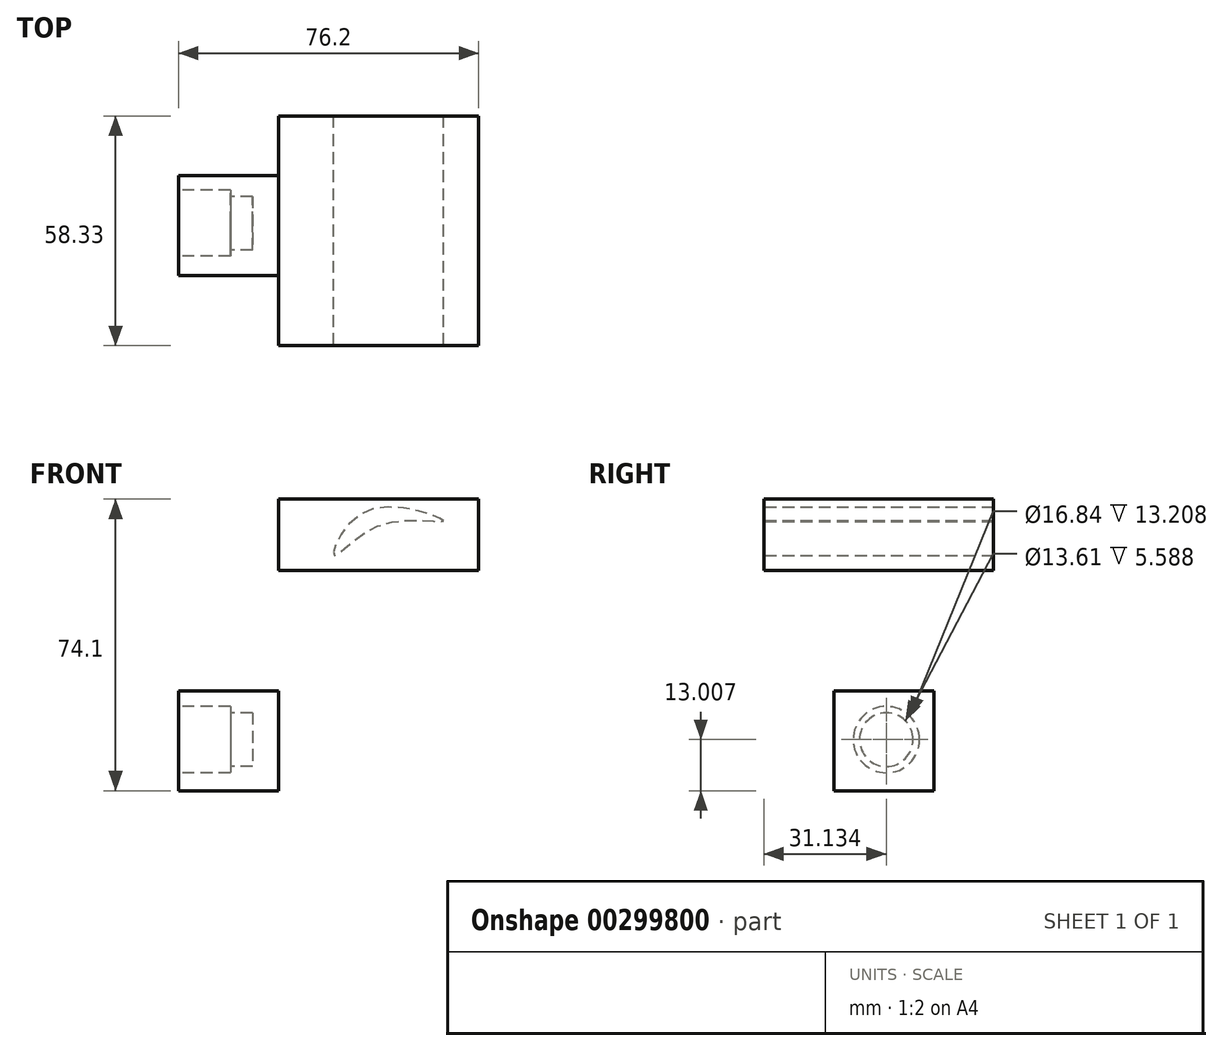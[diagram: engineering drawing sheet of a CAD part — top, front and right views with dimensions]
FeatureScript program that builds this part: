
annotation { "Feature Type Name" : "Feature", "Feature Type Description" : "" }
export const myFeature = defineFeature(function(context is Context, id is Id, definition is map)
    precondition{}
    {
        {
            var Q0;
            Q0=qCreatedBy(makeId("Front.planeOp"),FACE);
            var sketch = newSketch(context, id + "F0", { "sketchPlane" : qUnion([Q0])});
            skLineSegment(sketch, "E0", {"start": v(0, 25.4) * mm, "end": v(-25.4, 25.4) * mm});
            skLineSegment(sketch, "E1", {"start": v(0, 25.4) * mm, "end": v(0, 0) * mm});
            skLineSegment(sketch, "E2", {"start": v(0, 0) * mm, "end": v(-25.4, 0) * mm});
            skLineSegment(sketch, "E3", {"start": v(-25.4, 0) * mm, "end": v(-25.4, 25.4) * mm});
            skSolve(sketch);
        }
        {
            var Q0;
            Q0 = qSketchRegion(id + "F0", true);
            extrude(context, id + "F1", {"entities" : qUnion([Q0]), "depth" : 25.4 * mm});
        }
        {
            var Q0;
            Q0=makeQuery(id+"F0.imprint","IMPRINT",FACE,{"disambiguationData":[TD([[makeQuery(id+"F0.imprint","IMPRINT",EDGE,{"derivedFrom":sQuery(id+"F0.wireOp",EDGE,"E0")}),1.0]])]});
            extrude(context, id + "F2", {"entities" : qUnion([Q0]), "operationType" : NewBodyOperationType.ADD, "depth" : 25.4 * mm});
        }
        {
            var Q0;
            Q0=makeQuery(id+"F1.opExtrude","CAP_FACE",FACE,{"disambiguationData":[OSD([sQuery(id+"F0.wireOp",EDGE,"E0"),sQuery(id+"F0.wireOp",EDGE,"E1"),sQuery(id+"F0.wireOp",EDGE,"E2"),sQuery(id+"F0.wireOp",EDGE,"E3")])],"isStart":false});
            var sketch = newSketch(context, id + "F3", { "sketchPlane" : qUnion([Q0])});
            skCircle(sketch, "E4", {"center": v(-11.35, 11.82) * mm, "radius": 8.1 * mm});
            skCircle(sketch, "E5", {"center": v(-11.35, 11.82) * mm, "radius": 8.16 * mm});
            skSolve(sketch);
        }
        {
            var Q0;
            Q0 = qSketchRegion(id + "F3", true);
            var Q1;
            Q1=makeQuery(id+"F3.imprint","IMPRINT",FACE,{"disambiguationData":[TD([[makeQuery(id+"F3.imprint","IMPRINT",EDGE,{"derivedFrom":sQuery(id+"F3.wireOp",EDGE,"E4")}),1.0]])]});
            extrude(context, id + "F4", {"entities" : qUnion([Q0, Q1]), "operationType" : NewBodyOperationType.ADD, "oppositeDirection" : true, "depth" : 12.7 * mm});
        }
        {
            var Q0;
            Q0=makeQuery(id+"F1.opExtrude","SWEPT_FACE",FACE,{"disambiguationData":[OSD([sQuery(id+"F0.wireOp",EDGE,"E1")])]});
            var sketch = newSketch(context, id + "F5", { "sketchPlane" : qUnion([Q0])});
            skCircle(sketch, "E6", {"center": v(-13.12, 12.8) * mm, "radius": 9.62 * mm});
            skSolve(sketch);
        }
        {
            var Q0;
            Q0 = qSketchRegion(id + "F5", true);
            extrude(context, id + "F6", {"entities" : qUnion([Q0]), "operationType" : NewBodyOperationType.ADD, "oppositeDirection" : true, "depth" : 12.7 * mm});
        }
        {
            var Q0;
            Q0=makeQuery(id+"F1.opExtrude","SWEPT_FACE",FACE,{"disambiguationData":[OSD([sQuery(id+"F0.wireOp",EDGE,"E3")])]});
            var sketch = newSketch(context, id + "F7", { "sketchPlane" : qUnion([Q0])});
            skCircle(sketch, "E7", {"center": v(12.1, 13) * mm, "radius": 8.42 * mm});
            skSolve(sketch);
        }
        {
            var Q0;
            Q0 = qSketchRegion(id + "F7", true);
            extrude(context, id + "F8", {"entities" : qUnion([Q0]), "operationType" : NewBodyOperationType.REMOVE, "oppositeDirection" : true, "depth" : 13.2 * mm});
        }
        {
            var Q0;
            Q0=makeQuery(id+"F8.boolean.opBoolean","COPY",FACE,{"derivedFrom":makeQuery(id+"F8.opExtrude","CAP_FACE",FACE,{"disambiguationData":[OSD([sQuery(id+"F7.wireOp",EDGE,"E7")])],"isStart":false})});
            var sketch = newSketch(context, id + "F9", { "sketchPlane" : qUnion([Q0])});
            skCircle(sketch, "E8", {"center": v(12.1, 13) * mm, "radius": 6.8 * mm});
            skSolve(sketch);
        }
        {
            var Q0;
            Q0 = qSketchRegion(id + "F9", true);
            extrude(context, id + "F10", {"entities" : qUnion([Q0]), "operationType" : NewBodyOperationType.REMOVE, "oppositeDirection" : true, "depth" : 5.6 * mm});
        }
        {
            var Q0;
            Q0=qCreatedBy(makeId("Right.planeOp"),FACE);
            var sketch = newSketch(context, id + "F11", { "sketchPlane" : qUnion([Q0])});
            skLineSegment(sketch, "E9.bottom", {"start": v(-43.24, 55.97) * mm, "end": v(15.09, 55.97) * mm});
            skLineSegment(sketch, "E9.top", {"start": v(-43.24, 74.1) * mm, "end": v(15.09, 74.1) * mm});
            skLineSegment(sketch, "E9.left", {"start": v(-43.24, 55.97) * mm, "end": v(-43.24, 74.1) * mm});
            skLineSegment(sketch, "E9.right", {"start": v(15.09, 55.97) * mm, "end": v(15.09, 74.1) * mm});
            skPoint(sketch, "E9.middle", {"position": v(-14.08, 65.03) * mm});
            skSolve(sketch);
        }
        {
            var Q0;
            Q0 = qSketchRegion(id + "F11", true);
            extrude(context, id + "F12", {"entities" : qUnion([Q0]), "depth" : 50.8 * mm});
        }
        {
            var Q0;
            Q0=makeQuery(id+"F12.opExtrude","SWEPT_FACE",FACE,{"disambiguationData":[OSD([sQuery(id+"F11.wireOp",EDGE,"E9.right")])]});
            var sketch = newSketch(context, id + "F13", { "sketchPlane" : qUnion([Q0])});
            skFitSpline(sketch, "E10", {"points": [v(-41.9, 68.58) * mm, v(-22.58, 71.14) * mm, v(-14.1, 59.9) * mm, v(-26.13, 67.6) * mm, v(-41.9, 68.58) * mm]});
            skSolve(sketch);
        }
        {
            var Q0;
            Q0 = qSketchRegion(id + "F13", true);
            extrude(context, id + "F14", {"entities" : qUnion([Q0]), "operationType" : NewBodyOperationType.REMOVE, "oppositeDirection" : true, "depth" : 58.17 * mm});
        }
        {
            var Q0;
            Q0=qCreatedBy(makeId("Front.planeOp"),FACE);
            var sketch = newSketch(context, id + "F15", { "sketchPlane" : qUnion([Q0])});
            skCircle(sketch, "E11.cCircle", {"center": v(22.86, -28.97) * mm, "radius": 18.17 * mm, "construction": true});
            skLineSegment(sketch, "E11.0", {"start": v(35.67, -14.49) * mm, "end": v(41.98, -26.1) * mm});
            skLineSegment(sketch, "E11.1", {"start": v(41.98, -26.1) * mm, "end": v(39.34, -39.07) * mm});
            skLineSegment(sketch, "E11.2", {"start": v(39.34, -39.07) * mm, "end": v(29, -47.3) * mm});
            skLineSegment(sketch, "E11.3", {"start": v(29, -47.3) * mm, "end": v(15.78, -46.96) * mm});
            skLineSegment(sketch, "E11.4", {"start": v(15.78, -46.96) * mm, "end": v(5.87, -38.2) * mm});
            skLineSegment(sketch, "E11.5", {"start": v(5.87, -38.2) * mm, "end": v(3.92, -25.12) * mm});
            skLineSegment(sketch, "E11.6", {"start": v(3.92, -25.12) * mm, "end": v(10.82, -13.84) * mm});
            skLineSegment(sketch, "E11.7", {"start": v(10.82, -13.84) * mm, "end": v(23.36, -9.64) * mm});
            skLineSegment(sketch, "E11.8", {"start": v(23.36, -9.64) * mm, "end": v(35.67, -14.49) * mm});
            skPoint(sketch, "E11.0.midPoint", {"position": v(38.82, -20.3) * mm});
            skSolve(sketch);
        }
    });
